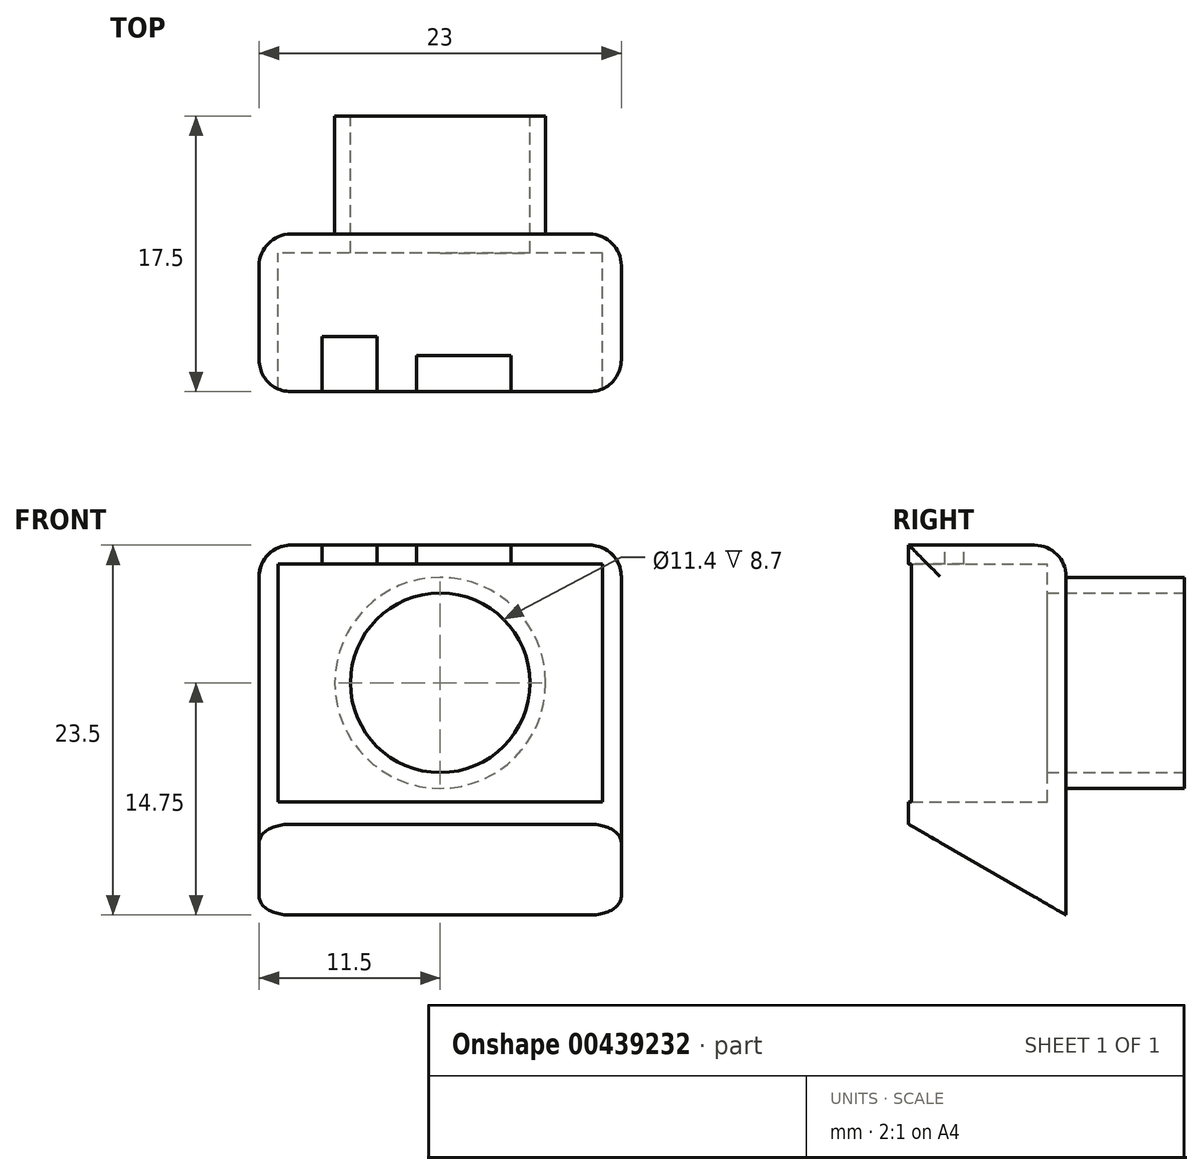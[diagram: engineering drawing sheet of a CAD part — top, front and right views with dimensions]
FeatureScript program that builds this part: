
annotation { "Feature Type Name" : "Feature", "Feature Type Description" : "" }
export const myFeature = defineFeature(function(context is Context, id is Id, definition is map)
    precondition{}
    {
        {
            var Q0;
            Q0=qCreatedBy(makeId("Front.planeOp"),FACE);
            var sketch = newSketch(context, id + "F0", { "sketchPlane" : qUnion([Q0])});
            skLineSegment(sketch, "E0.bottom", {"start": v(11.5, -8.75) * mm, "end": v(-11.5, -8.75) * mm});
            skLineSegment(sketch, "E0.top", {"start": v(11.5, 8.75) * mm, "end": v(-11.5, 8.75) * mm});
            skLineSegment(sketch, "E0.left", {"start": v(11.5, -8.75) * mm, "end": v(11.5, 8.75) * mm});
            skLineSegment(sketch, "E0.right", {"start": v(-11.5, -8.75) * mm, "end": v(-11.5, 8.75) * mm});
            skPoint(sketch, "E0.middle", {"position": v(0, 0) * mm});
            skSolve(sketch);
        }
        {
            var Q0;
            Q0=qSketchRegion(id+"F0",true);
            extrude(context, id + "F1", {"entities" : qUnion([Q0]), "depth" : 10 * mm, "offsetDistance" : 25 * mm});
        }
        {
            var Q0;
            Q0=makeQuery(id+"F1.opExtrude","CAP_FACE",FACE,{"disambiguationData":[OSD([sQuery(id+"F0.wireOp",EDGE,"E0.bottom"),sQuery(id+"F0.wireOp",EDGE,"E0.top"),sQuery(id+"F0.wireOp",EDGE,"E0.left"),sQuery(id+"F0.wireOp",EDGE,"E0.right")])],"isStart":false});
            shell(context, id + "F2", {"entities" : qUnion([Q0]), "thickness" : 1.2 * mm});
        }
        {
            var Q0;
            Q0=makeQuery(id+"F1.opExtrude","CAP_FACE",FACE,{"disambiguationData":[OSD([sQuery(id+"F0.wireOp",EDGE,"E0.bottom"),sQuery(id+"F0.wireOp",EDGE,"E0.top"),sQuery(id+"F0.wireOp",EDGE,"E0.left"),sQuery(id+"F0.wireOp",EDGE,"E0.right")])],"isStart":true});
            var sketch = newSketch(context, id + "F3", { "sketchPlane" : qUnion([Q0])});
            skCircle(sketch, "E1", {"center": v(0, 0) * mm, "radius": 5.7 * mm});
            skCircle(sketch, "E2.0", {"center": v(0, 0) * mm, "radius": 6.7 * mm});
            skSolve(sketch);
        }
        {
            var Q0;
            Q0=makeQuery(id+"F3.imprint","IMPRINT",FACE,{"disambiguationData":[TD([[makeQuery(id+"F3.imprint","IMPRINT",EDGE,{"derivedFrom":sQuery(id+"F3.wireOp",EDGE,"E1")}),1.0]])]});
            extrude(context, id + "F4", {"entities" : qUnion([Q0]), "operationType" : NewBodyOperationType.REMOVE, "oppositeDirection" : true, "depth" : 3 * mm, "offsetDistance" : 25 * mm});
        }
        {
            var Q0;
            Q0=makeQuery(id+"F3.imprint","IMPRINT",FACE,{"disambiguationData":[TD([[makeQuery(id+"F3.imprint","IMPRINT",EDGE,{"derivedFrom":sQuery(id+"F3.wireOp",EDGE,"E1")}),-1.0]])]});
            extrude(context, id + "F5", {"entities" : qUnion([Q0]), "operationType" : NewBodyOperationType.ADD, "depth" : 7.5 * mm, "offsetDistance" : 25 * mm});
        }
        {
            var Q0;
            Q0=makeQuery(id+"F1.opExtrude","SWEPT_FACE",FACE,{"disambiguationData":[OSD([sQuery(id+"F0.wireOp",EDGE,"E0.top")])]});
            var sketch = newSketch(context, id + "F6", { "sketchPlane" : qUnion([Q0])});
            skLineSegment(sketch, "E3.bottom", {"start": v(4.5, -10) * mm, "end": v(-1.5, -10) * mm});
            skLineSegment(sketch, "E3.top", {"start": v(4.5, -7.7) * mm, "end": v(-1.5, -7.7) * mm});
            skLineSegment(sketch, "E3.left", {"start": v(4.5, -10) * mm, "end": v(4.5, -7.7) * mm});
            skLineSegment(sketch, "E3.right", {"start": v(-1.5, -10) * mm, "end": v(-1.5, -7.7) * mm});
            skLineSegment(sketch, "E4.bottom", {"start": v(-1.5, -7.7) * mm, "end": v(4.5, -7.7) * mm});
            skLineSegment(sketch, "E4.top", {"start": v(-1.5, -5.4) * mm, "end": v(4.5, -5.4) * mm});
            skLineSegment(sketch, "E4.left", {"start": v(-1.5, -7.7) * mm, "end": v(-1.5, -5.4) * mm});
            skLineSegment(sketch, "E4.right", {"start": v(4.5, -7.7) * mm, "end": v(4.5, -5.4) * mm});
            skLineSegment(sketch, "E5.bottom", {"start": v(-7.5, -10) * mm, "end": v(-4, -10) * mm});
            skLineSegment(sketch, "E5.top", {"start": v(-7.5, -6.5) * mm, "end": v(-4, -6.5) * mm});
            skLineSegment(sketch, "E5.left", {"start": v(-7.5, -10) * mm, "end": v(-7.5, -6.5) * mm});
            skLineSegment(sketch, "E5.right", {"start": v(-4, -10) * mm, "end": v(-4, -6.5) * mm});
            skSolve(sketch);
        }
        {
            var Q0;
            Q0=makeQuery(id+"F6.imprint","IMPRINT",FACE,{"disambiguationData":[TD([[makeQuery(id+"F6.imprint","IMPRINT",EDGE,{"derivedFrom":sQuery(id+"F6.wireOp",EDGE,"E3.bottom")}),-1.0]])]});
            var Q1;
            Q1=makeQuery(id+"F6.imprint","IMPRINT",FACE,{"disambiguationData":[TD([[makeQuery(id+"F6.imprint","IMPRINT",EDGE,{"derivedFrom":sQuery(id+"F6.wireOp",EDGE,"E5.bottom")}),-1.0]])]});
            extrude(context, id + "F7", {"entities" : qUnion([Q0, Q1]), "operationType" : NewBodyOperationType.REMOVE, "oppositeDirection" : true, "depth" : 4 * mm, "offsetDistance" : 25 * mm});
        }
        {
            var Q0;
            Q0=makeQuery(id+"F1.opExtrude","SWEPT_FACE",FACE,{"disambiguationData":[OSD([sQuery(id+"F0.wireOp",EDGE,"E0.bottom")])]});
            extrude(context, id + "F8", {"entities" : qUnion([Q0]), "operationType" : NewBodyOperationType.ADD, "depth" : 6 * mm, "offsetDistance" : 25 * mm});
        }
        {
            var Q0;
            {var subQ0=sQuery(id+"F0.wireOp",EDGE,"E0.left");Q0=makeQuery(id+"F8.boolean.opBoolean","MERGE",FACE,{"derivedFrom":[makeQuery(id+"F1.opExtrude","SWEPT_FACE",FACE,{"disambiguationData":[OSD([subQ0])]}),makeQuery(id+"F8.opExtrude","SWEPT_FACE",FACE,{"disambiguationData":[OSD([sQuery(id+"F0.wireOp",EDGE,"E0.bottom"),subQ0])]})]});}
            var sketch = newSketch(context, id + "F9", { "sketchPlane" : qUnion([Q0])});
            skLineSegment(sketch, "E6", {"start": v(0, -14.75) * mm, "end": v(-10, -8.98) * mm});
            skSolve(sketch);
        }
        {
            var Q0;
            {var subQ0=sQuery(id+"F9.wireOp",EDGE,"E6");Q0=makeQuery(id+"F9.imprint","IMPRINT",FACE,{"disambiguationData":[TD([[makeQuery(id+"F9.imprint","IMPRINT",EDGE,{"derivedFrom":subQ0}),1.0]])]});}
            extrude(context, id + "F10", {"entities" : qUnion([Q0]), "operationType" : NewBodyOperationType.REMOVE, "oppositeDirection" : true, "depth" : 30 * mm, "offsetDistance" : 25 * mm});
        }
        {
            var Q0;
            Q0=makeQuery(id+"F1.opExtrude","CAP_EDGE",EDGE,{"disambiguationData":[OSD([sQuery(id+"F0.wireOp",EDGE,"E0.top")])],"isStart":true});
            var Q1;
            {var subQ0=sQuery(id+"F0.wireOp",EDGE,"E0.right");var subQ1=sQuery(id+"F0.wireOp",EDGE,"E0.bottom");Q1=makeQuery(id+"F8.boolean.opBoolean","MERGE",EDGE,{"derivedFrom":[makeQuery(id+"F1.opExtrude","CAP_EDGE",EDGE,{"disambiguationData":[OSD([subQ0])],"isStart":true}),makeQuery(id+"F8.opExtrude","SWEPT_EDGE",EDGE,{"disambiguationData":[OSD([subQ1,subQ0]),TDD([makeQuery(id+"F1.opExtrude","CAP_VERTEX",VERTEX,{"disambiguationData":[OSD([subQ1,subQ0])],"isStart":true})])]})]});}
            var Q2;
            {var subQ0=sQuery(id+"F0.wireOp",EDGE,"E0.left");var subQ1=sQuery(id+"F0.wireOp",EDGE,"E0.bottom");Q2=makeQuery(id+"F8.boolean.opBoolean","MERGE",EDGE,{"derivedFrom":[makeQuery(id+"F1.opExtrude","CAP_EDGE",EDGE,{"disambiguationData":[OSD([subQ0])],"isStart":true}),makeQuery(id+"F8.opExtrude","SWEPT_EDGE",EDGE,{"disambiguationData":[OSD([subQ1,subQ0]),TDD([makeQuery(id+"F1.opExtrude","CAP_VERTEX",VERTEX,{"disambiguationData":[OSD([subQ1,subQ0])],"isStart":true})])]})]});}
            var Q3;
            Q3=makeQuery(id+"F1.opExtrude","SWEPT_EDGE",EDGE,{"disambiguationData":[OSD([sQuery(id+"F0.wireOp",EDGE,"E0.top"),sQuery(id+"F0.wireOp",EDGE,"E0.left")])]});
            var Q4;
            Q4=makeQuery(id+"F1.opExtrude","SWEPT_EDGE",EDGE,{"disambiguationData":[OSD([sQuery(id+"F0.wireOp",EDGE,"E0.top"),sQuery(id+"F0.wireOp",EDGE,"E0.right")])]});
            var Q5;
            {var subQ0=sQuery(id+"F0.wireOp",EDGE,"E0.right");var subQ1=sQuery(id+"F0.wireOp",EDGE,"E0.bottom");Q5=makeQuery(id+"F8.boolean.opBoolean","MERGE",EDGE,{"derivedFrom":[makeQuery(id+"F1.opExtrude","CAP_EDGE",EDGE,{"disambiguationData":[OSD([subQ0])],"isStart":false}),makeQuery(id+"F8.opExtrude","SWEPT_EDGE",EDGE,{"disambiguationData":[OSD([subQ1,subQ0]),TDD([makeQuery(id+"F1.opExtrude","CAP_VERTEX",VERTEX,{"disambiguationData":[OSD([subQ1,subQ0])],"isStart":false})])]})]});}
            var Q6;
            {var subQ0=sQuery(id+"F0.wireOp",EDGE,"E0.left");var subQ1=sQuery(id+"F0.wireOp",EDGE,"E0.bottom");Q6=makeQuery(id+"F8.boolean.opBoolean","MERGE",EDGE,{"derivedFrom":[makeQuery(id+"F1.opExtrude","CAP_EDGE",EDGE,{"disambiguationData":[OSD([subQ0])],"isStart":false}),makeQuery(id+"F8.opExtrude","SWEPT_EDGE",EDGE,{"disambiguationData":[OSD([subQ1,subQ0]),TDD([makeQuery(id+"F1.opExtrude","CAP_VERTEX",VERTEX,{"disambiguationData":[OSD([subQ1,subQ0])],"isStart":false})])]})]});}
            fillet(context, id + "F11", {"entities" : qUnion([Q0, Q1, Q2, Q3, Q4, Q5, Q6]), "radius" : 2 * mm, "tangentPropagation" : true, "allowEdgeOverflow" : false});
        }
    });
